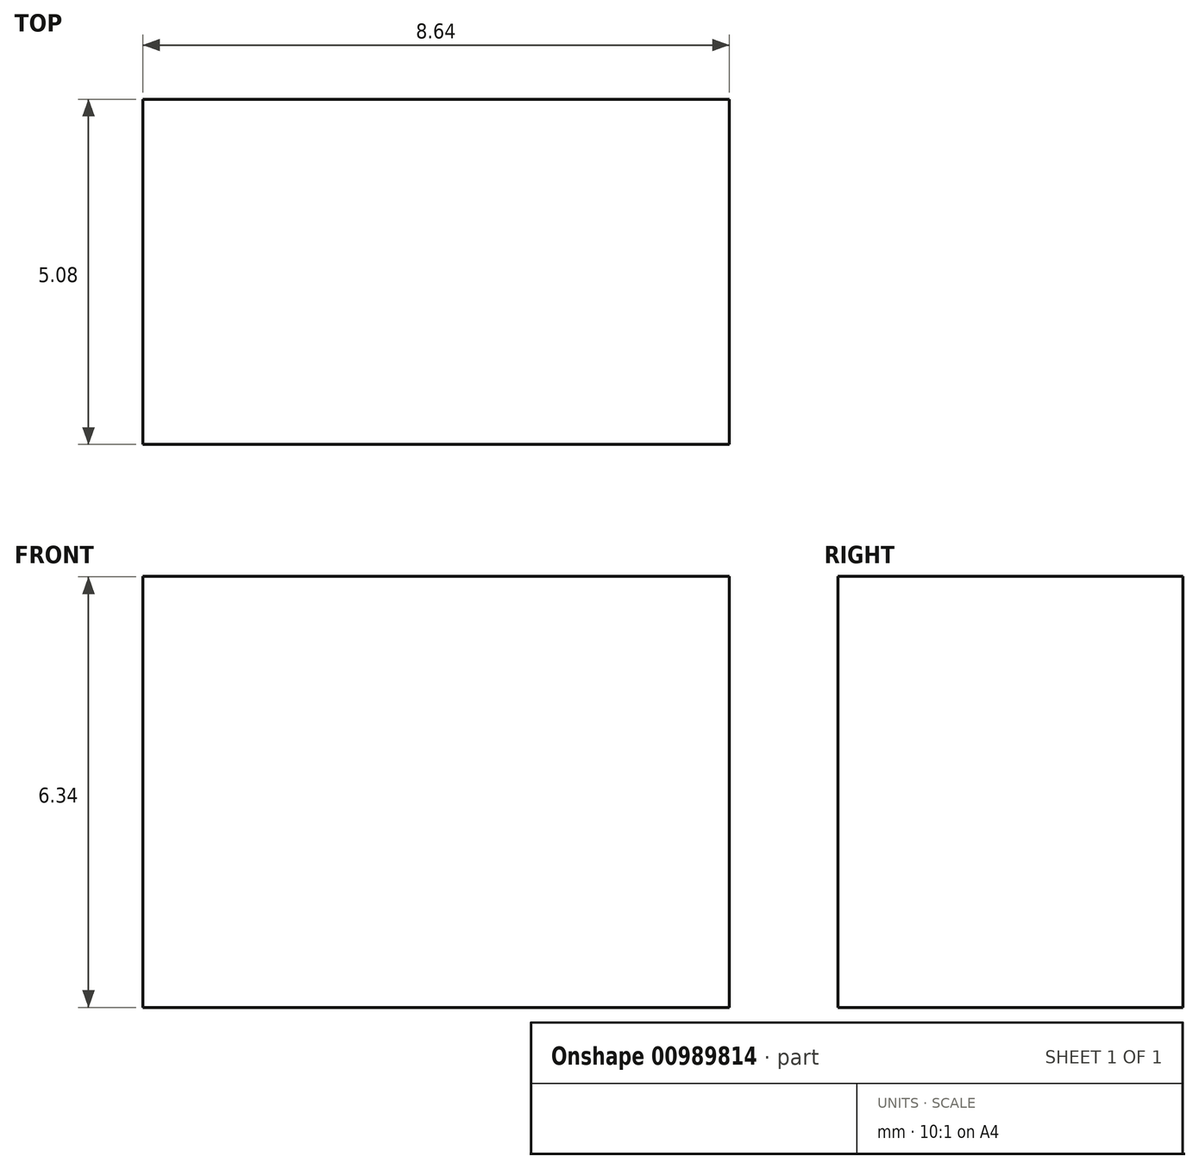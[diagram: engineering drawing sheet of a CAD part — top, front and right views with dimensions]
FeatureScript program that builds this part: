
annotation { "Feature Type Name" : "Feature", "Feature Type Description" : "" }
export const myFeature = defineFeature(function(context is Context, id is Id, definition is map)
    precondition{}
    {
        {
            var Q0;
            Q0=qCreatedBy(makeId("Top.planeOp"),FACE);
            var sketch = newSketch(context, id + "F0", { "sketchPlane" : qUnion([Q0])});
            skLineSegment(sketch, "E0.bottom", {"start": v(-4.32, -2.54) * mm, "end": v(4.32, -2.54) * mm});
            skLineSegment(sketch, "E0.top", {"start": v(-4.32, 2.54) * mm, "end": v(4.32, 2.54) * mm});
            skLineSegment(sketch, "E0.left", {"start": v(-4.32, -2.54) * mm, "end": v(-4.32, 2.54) * mm});
            skLineSegment(sketch, "E0.right", {"start": v(4.32, -2.54) * mm, "end": v(4.32, 2.54) * mm});
            skLineSegment(sketch, "E1", {"start": v(-4.32, -2.54) * mm, "end": v(4.32, 2.54) * mm, "construction": true});
            skSolve(sketch);
        }
        {
            var Q0;
            Q0 = qSketchRegion(id + "F0", true);
            extrude(context, id + "F1", {"entities" : qUnion([Q0]), "endBound" : BoundingType.SYMMETRIC, "depth" : 6.35 * mm, "offsetDistance" : 25.4 * mm});
        }
    });
